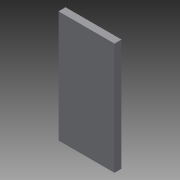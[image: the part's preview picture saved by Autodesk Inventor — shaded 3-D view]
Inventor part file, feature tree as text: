
AUTODESK INVENTOR PART (.ipt)
format: ipt  version: 2013 (Build 170138000, 138)  size: 66,048 bytes
history: native  units: in
note: dims shown in document units (in); Inventor stores cm internally (conversion verified against a paired STEP export)
features: extrude x1, sketch x1
ambient origin geometry x8: Origin, YZ Plane, XZ Plane, XY Plane, X Axis, Y Axis, Z Axis, Center Point
bodies: Solid1 (feature_tree)
feature tree (2):
  extrude  "Extrusion1"  Depth=2.0in
  sketch  "Sketch1"  dims[d0=1.0in d1=2.0in d2=0.125in d3=0.0in]
